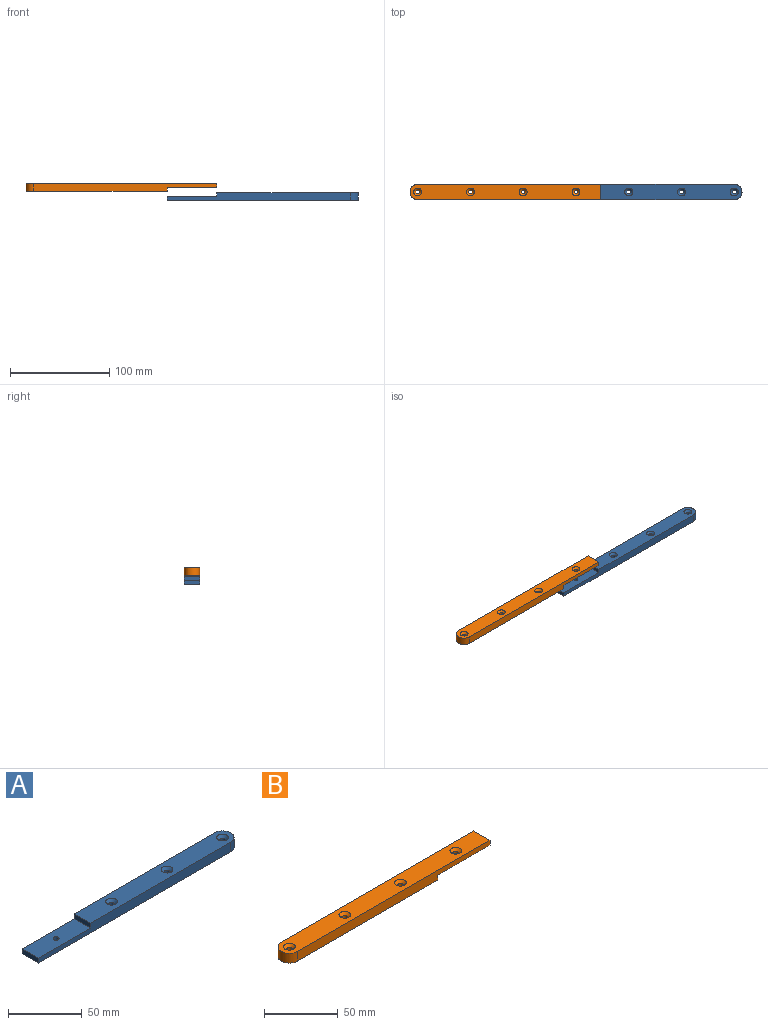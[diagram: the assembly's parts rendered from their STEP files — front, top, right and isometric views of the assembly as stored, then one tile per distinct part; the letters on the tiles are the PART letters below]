
ASSEMBLY  parts=2 mates=1
PART A: 15 faces, bbox 192.5x15.5x8 mm
  f0: plane 15.5x4mm, normal (-1,0,0), area 62mm2, adj f2,f12,f13,f14
  f1: plane 15.5x4mm, normal (-1,0,0), area 62mm2, adj f2,f11,f13,f14
  f2: plane 50x15.5mm, normal (0,0,1), area 762.4mm2, adj f0,f1,f10,f13,f14
  f3: cone r=2mm half-angle=45deg, axis (0,0,1), area 53.3mm2, adj f9,f12
  f4: cone r=2mm half-angle=45deg, axis (0,0,1), area 53.3mm2, adj f8,f12
  f5: cone r=2mm half-angle=45deg, axis (0,0,1), area 53.3mm2, adj f7,f12
  f6: cylinder r=7.75mm len=15.5mm, axis (0,0,-1), area 194.8mm2, adj f11,f12,f13,f14
  f7: cylinder r=2mm len=6mm, axis (0,0,1), area 75.4mm2, adj f5,f11
  f8: cylinder r=2mm len=6mm, axis (0,0,1), area 75.4mm2, adj f4,f11
  f9: cylinder r=2mm len=6mm, axis (0,0,1), area 75.4mm2, adj f3,f11
  f10: cylinder r=2mm len=4mm, axis (0,0,1), area 50.3mm2, adj f2,f11
  f11: plane 192.5x15.5mm, normal (0,0,-1), area 2907.7mm2, adj f1,f6,f7,f8,f9,f10,f13,f14
  f12: plane 142.5x15.5mm, normal (0,0,1), area 2032.2mm2, adj f0,f3,f4,f5,f6,f13,f14
  f13: plane 184.75x8mm, normal (0,-1,0), area 1278mm2, adj f0,f1,f2,f6,f11,f12
  f14: plane 184.75x8mm, normal (0,1,0), area 1278mm2, adj f0,f1,f2,f6,f11,f12
PART B: 16 faces, bbox 192.5x15.5x8 mm
  f0: plane 184.75x8mm, normal (0,1,0), area 1278mm2, adj f1,f3,f4,f13,f14,f15
  f1: cylinder r=7.75mm len=15.5mm, axis (0,0,-1), area 194.8mm2, adj f0,f2,f3,f4
  f2: plane 184.75x8mm, normal (0,-1,0), area 1278mm2, adj f1,f3,f4,f13,f14,f15
  f3: plane 192.5x15.5mm, normal (0,0,1), area 2756.9mm2, adj f0,f1,f2,f9,f10,f11,f12,f13
  f4: plane 142.5x15.5mm, normal (0,0,-1), area 2145.3mm2, adj f0,f1,f2,f6,f7,f8,f14
  f5: cylinder r=2mm len=4mm, axis (0,0,1), area 25.1mm2, adj f9,f15
  f6: cylinder r=2mm len=6mm, axis (0,0,1), area 75.4mm2, adj f4,f10
  f7: cylinder r=2mm len=6mm, axis (0,0,1), area 75.4mm2, adj f4,f11
  f8: cylinder r=2mm len=6mm, axis (0,0,1), area 75.4mm2, adj f4,f12
  f9: cone r=2mm half-angle=45deg, axis (0,0,1), area 53.3mm2, adj f3,f5
  f10: cone r=2mm half-angle=45deg, axis (0,0,1), area 53.3mm2, adj f3,f6
  f11: cone r=2mm half-angle=45deg, axis (0,0,1), area 53.3mm2, adj f3,f7
  f12: cone r=2mm half-angle=45deg, axis (0,0,1), area 53.3mm2, adj f3,f8
  f13: plane 15.5x4mm, normal (1,0,0), area 62mm2, adj f0,f2,f3,f15
  f14: plane 15.5x4mm, normal (1,0,0), area 62mm2, adj f0,f2,f4,f15
  f15: plane 50x15.5mm, normal (0,0,-1), area 762.4mm2, adj f0,f2,f5,f13,f14
PLACE A t=(-31.44,-35.25,32.05)mm
PLACE B t=(-31.44,-35.25,41.15)mm
MATE parallel A.f10 <-> B.f5  axis (0,0,1) through (-31.44,-35.25,36.05)mm
